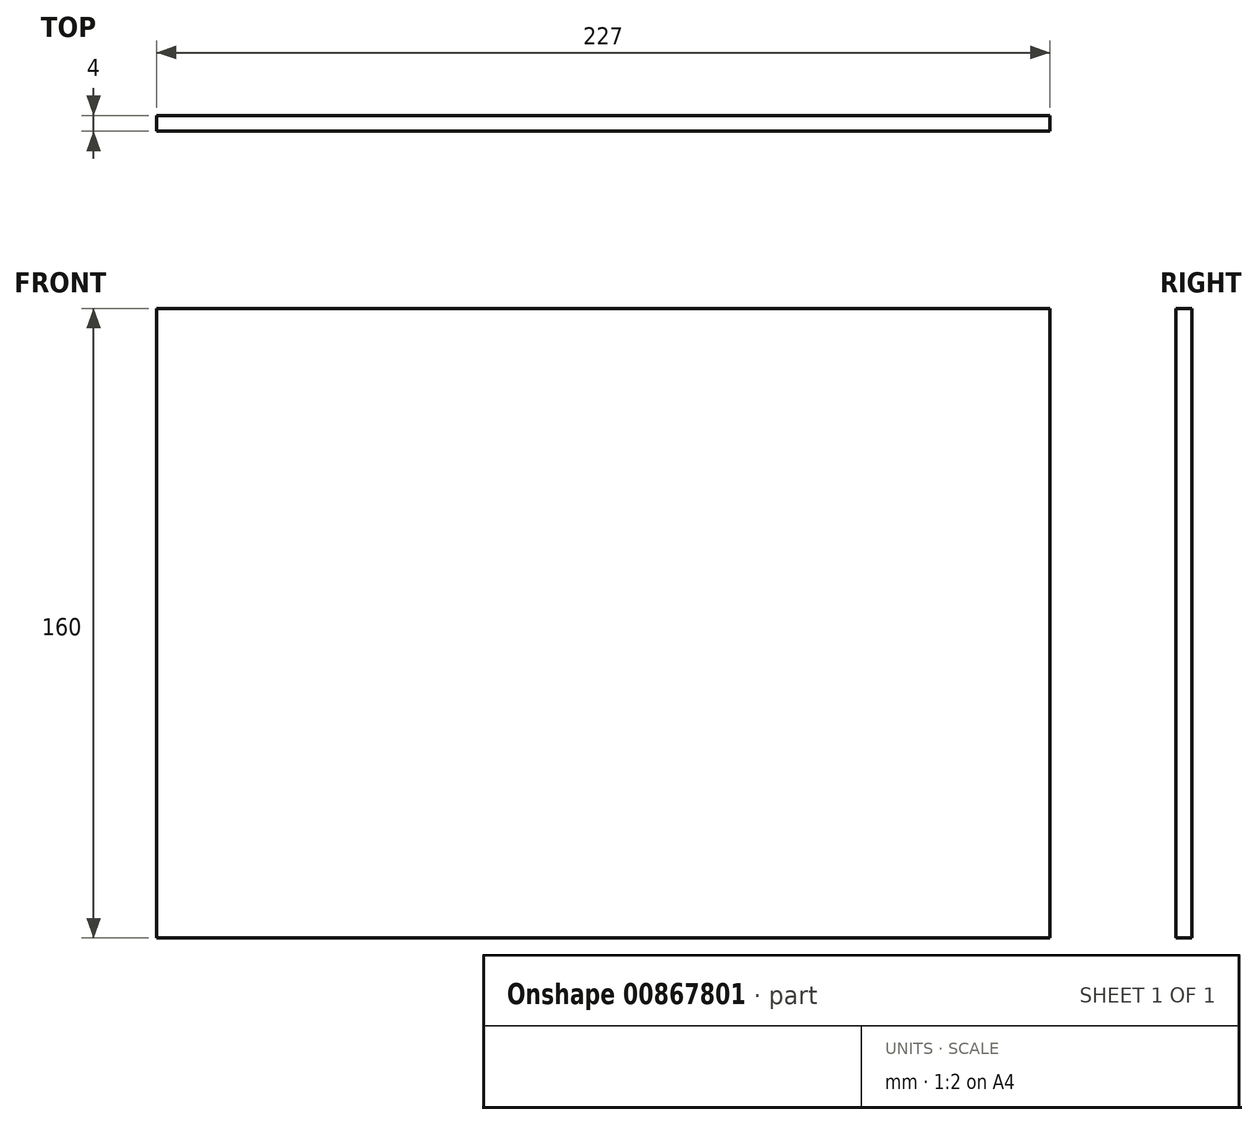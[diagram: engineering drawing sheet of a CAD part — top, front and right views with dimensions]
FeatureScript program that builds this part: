
annotation { "Feature Type Name" : "Feature", "Feature Type Description" : "" }
export const myFeature = defineFeature(function(context is Context, id is Id, definition is map)
    precondition{}
    {
        {
            var Q0;
            Q0=qCreatedBy(makeId("Front.planeOp"),FACE);
            var sketch = newSketch(context, id + "F0", { "sketchPlane" : qUnion([Q0])});
            skLineSegment(sketch, "E0.bottom", {"start": v(-227, 160) * mm, "end": v(0, 160) * mm});
            skLineSegment(sketch, "E0.top", {"start": v(-227, 0) * mm, "end": v(0, 0) * mm});
            skLineSegment(sketch, "E0.left", {"start": v(-227, 160) * mm, "end": v(-227, 0) * mm});
            skLineSegment(sketch, "E0.right", {"start": v(0, 160) * mm, "end": v(0, 0) * mm});
            skSolve(sketch);
        }
        {
            var Q0;
            Q0=makeQuery(id+"F0.imprint","IMPRINT",FACE,{"disambiguationData":[TD([[makeQuery(id+"F0.imprint","IMPRINT",EDGE,{"derivedFrom":sQuery(id+"F0.wireOp",EDGE,"E0.bottom")}),-1.0]])]});
            extrude(context, id + "F1", {"entities" : qUnion([Q0]), "depth" : 4 * mm, "offsetDistance" : 25.4 * mm});
        }
    });
